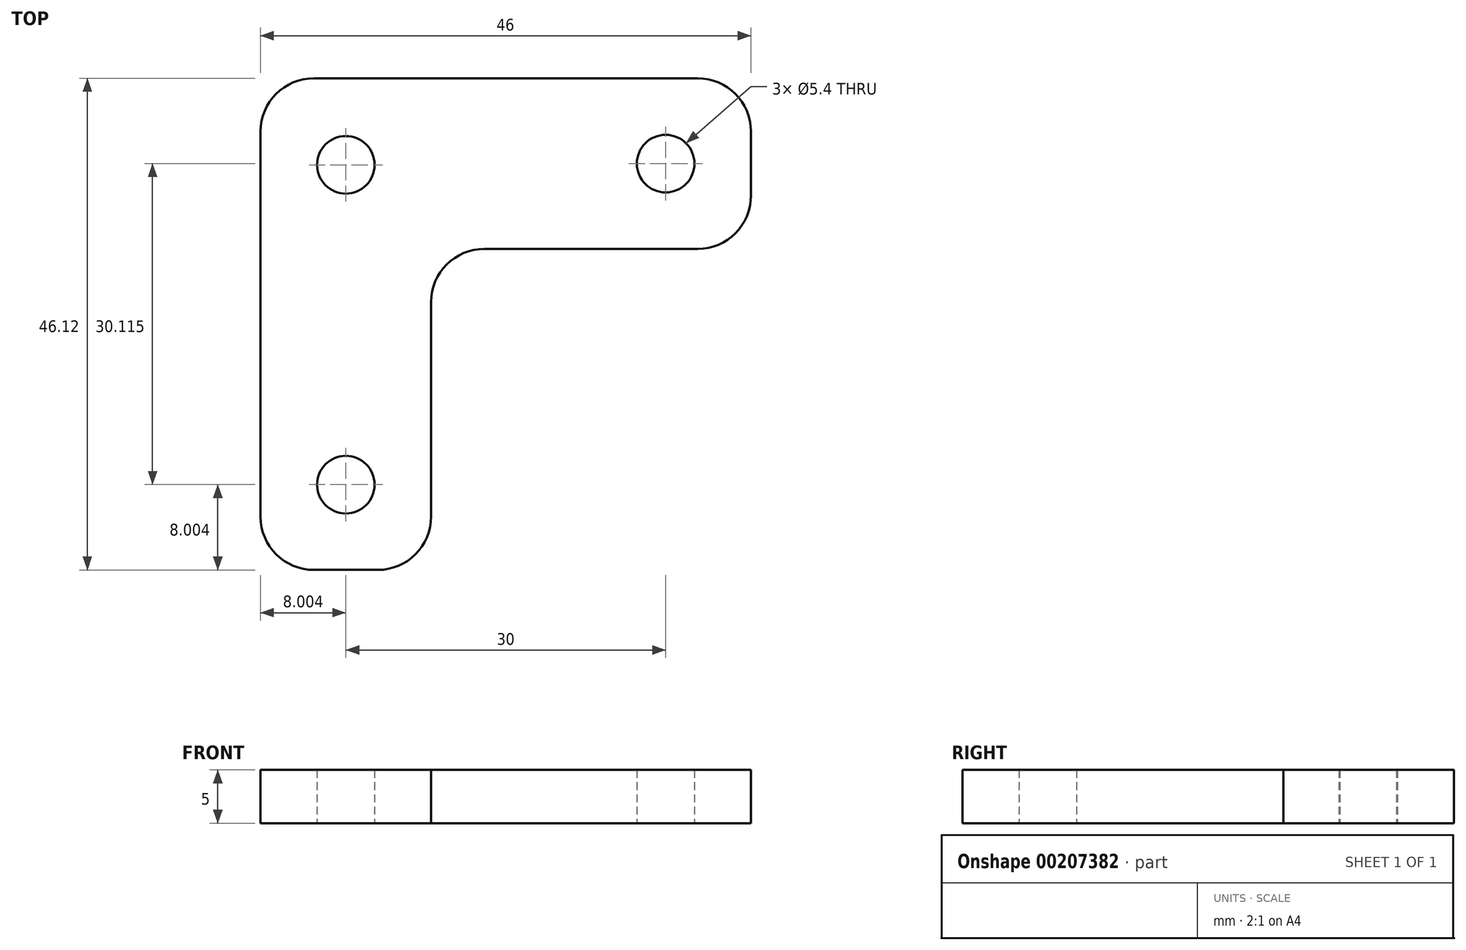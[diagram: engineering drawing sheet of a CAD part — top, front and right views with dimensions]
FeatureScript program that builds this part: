
annotation { "Feature Type Name" : "Feature", "Feature Type Description" : "" }
export const myFeature = defineFeature(function(context is Context, id is Id, definition is map)
    precondition{}
    {
        {
            var Q0;
            Q0=qCreatedBy(makeId("Top.planeOp"),FACE);
            var sketch = newSketch(context, id + "F0", { "sketchPlane" : qUnion([Q0])});
            skLineSegment(sketch, "E0.bottom", {"start": v(-20.79, 25.5) * mm, "end": v(25.21, 25.5) * mm});
            skLineSegment(sketch, "E0.left", {"start": v(-20.79, 25.5) * mm, "end": v(-20.79, -20.62) * mm});
            skCircle(sketch, "E1", {"center": v(-12.79, 17.38) * mm, "radius": 2.7 * mm});
            skCircle(sketch, "E2", {"center": v(17.21, 17.5) * mm, "radius": 2.7 * mm});
            skCircle(sketch, "E3", {"center": v(-12.79, -12.62) * mm, "radius": 2.7 * mm});
            skLineSegment(sketch, "E4", {"start": v(-12.79, 17.38) * mm, "end": v(17.21, 17.5) * mm, "construction": true});
            skPoint(sketch, "E5", {"position": v(2.21, 17.44) * mm});
            skPoint(sketch, "E6", {"position": v(2.21, 25.5) * mm});
            skLineSegment(sketch, "E7", {"start": v(-20.79, -20.62) * mm, "end": v(-4.79, -20.62) * mm});
            skLineSegment(sketch, "E8", {"start": v(-4.79, -20.62) * mm, "end": v(-4.79, 9.5) * mm});
            skLineSegment(sketch, "E9", {"start": v(-4.79, 9.5) * mm, "end": v(25.21, 9.5) * mm});
            skLineSegment(sketch, "E10", {"start": v(25.21, 9.5) * mm, "end": v(25.21, 25.5) * mm});
            skPoint(sketch, "E11", {"position": v(25.21, 17.5) * mm});
            skPoint(sketch, "E12", {"position": v(-12.79, -20.62) * mm});
            skSolve(sketch);
        }
        {
            var Q0;
            Q0=makeQuery(id+"F0.imprint","IMPRINT",FACE,{"disambiguationData":[TD([[makeQuery(id+"F0.imprint","IMPRINT",EDGE,{"derivedFrom":sQuery(id+"F0.wireOp",EDGE,"E0.bottom")}),-1.0]])]});
            extrude(context, id + "F1", {"entities" : qUnion([Q0]), "depth" : 5 * mm});
        }
        {
            var Q0;
            Q0=makeQuery(id+"F1.opExtrude","SWEPT_EDGE",EDGE,{"disambiguationData":[OSD([sQuery(id+"F0.wireOp",EDGE,"E0.left"),sQuery(id+"F0.wireOp",EDGE,"E7")])]});
            var Q1;
            Q1=makeQuery(id+"F1.opExtrude","SWEPT_EDGE",EDGE,{"disambiguationData":[OSD([sQuery(id+"F0.wireOp",EDGE,"E7"),sQuery(id+"F0.wireOp",EDGE,"E8")])]});
            var Q2;
            Q2=makeQuery(id+"F1.opExtrude","SWEPT_EDGE",EDGE,{"disambiguationData":[OSD([sQuery(id+"F0.wireOp",EDGE,"E9"),sQuery(id+"F0.wireOp",EDGE,"E10")])]});
            var Q3;
            Q3=makeQuery(id+"F1.opExtrude","SWEPT_EDGE",EDGE,{"disambiguationData":[OSD([sQuery(id+"F0.wireOp",EDGE,"E0.bottom"),sQuery(id+"F0.wireOp",EDGE,"E10")])]});
            var Q4;
            Q4=makeQuery(id+"F1.opExtrude","SWEPT_EDGE",EDGE,{"disambiguationData":[OSD([sQuery(id+"F0.wireOp",EDGE,"E0.bottom"),sQuery(id+"F0.wireOp",EDGE,"E0.left")])]});
            var Q5;
            Q5=makeQuery(id+"F1.opExtrude","SWEPT_EDGE",EDGE,{"disambiguationData":[OSD([sQuery(id+"F0.wireOp",EDGE,"E8"),sQuery(id+"F0.wireOp",EDGE,"E9")])]});
            fillet(context, id + "F2", {"entities" : qUnion([Q0, Q1, Q2, Q3, Q4, Q5]), "radius" : 5 * mm, "tangentPropagation" : true, "allowEdgeOverflow" : false});
        }
    });
